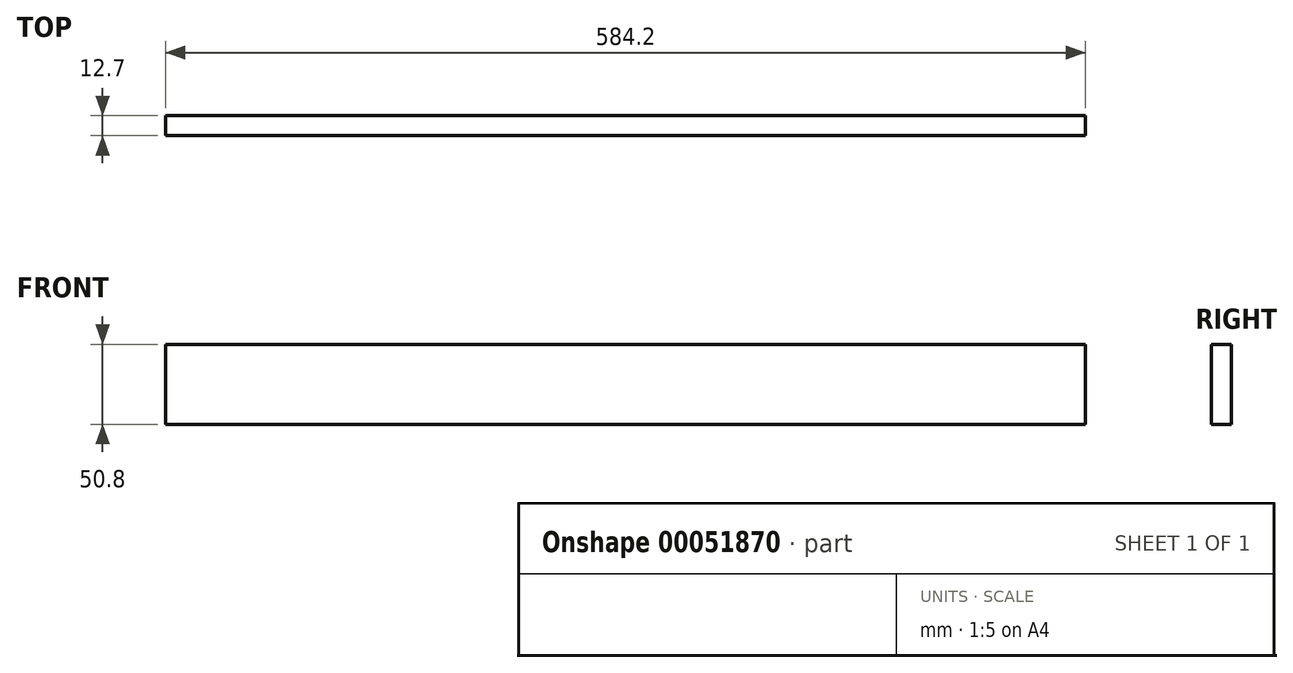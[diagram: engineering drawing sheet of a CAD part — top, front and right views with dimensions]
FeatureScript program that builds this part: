
annotation { "Feature Type Name" : "Feature", "Feature Type Description" : "" }
export const myFeature = defineFeature(function(context is Context, id is Id, definition is map)
    precondition{}
    {
        {
            var Q0;
            Q0=qCreatedBy(makeId("Front.planeOp"),FACE);
            var sketch = newSketch(context, id + "F0", { "sketchPlane" : qUnion([Q0])});
            skLineSegment(sketch, "E0.bottom", {"start": v(-292.1, 25.4) * mm, "end": v(292.1, 25.4) * mm});
            skLineSegment(sketch, "E0.top", {"start": v(-292.1, -25.4) * mm, "end": v(292.1, -25.4) * mm});
            skLineSegment(sketch, "E0.left", {"start": v(-292.1, 25.4) * mm, "end": v(-292.1, -25.4) * mm});
            skLineSegment(sketch, "E0.right", {"start": v(292.1, 25.4) * mm, "end": v(292.1, -25.4) * mm});
            skSolve(sketch);
        }
        {
            var Q0;
            Q0=makeQuery(id+"F0.imprint","IMPRINT",FACE,{"disambiguationData":[TD([[makeQuery(id+"F0.imprint","IMPRINT",EDGE,{"derivedFrom":sQuery(id+"F0.wireOp",EDGE,"E0.bottom")}),-1.0]])]});
            extrude(context, id + "F1", {"entities" : qUnion([Q0]), "depth" : 12.7 * mm});
        }
    });
